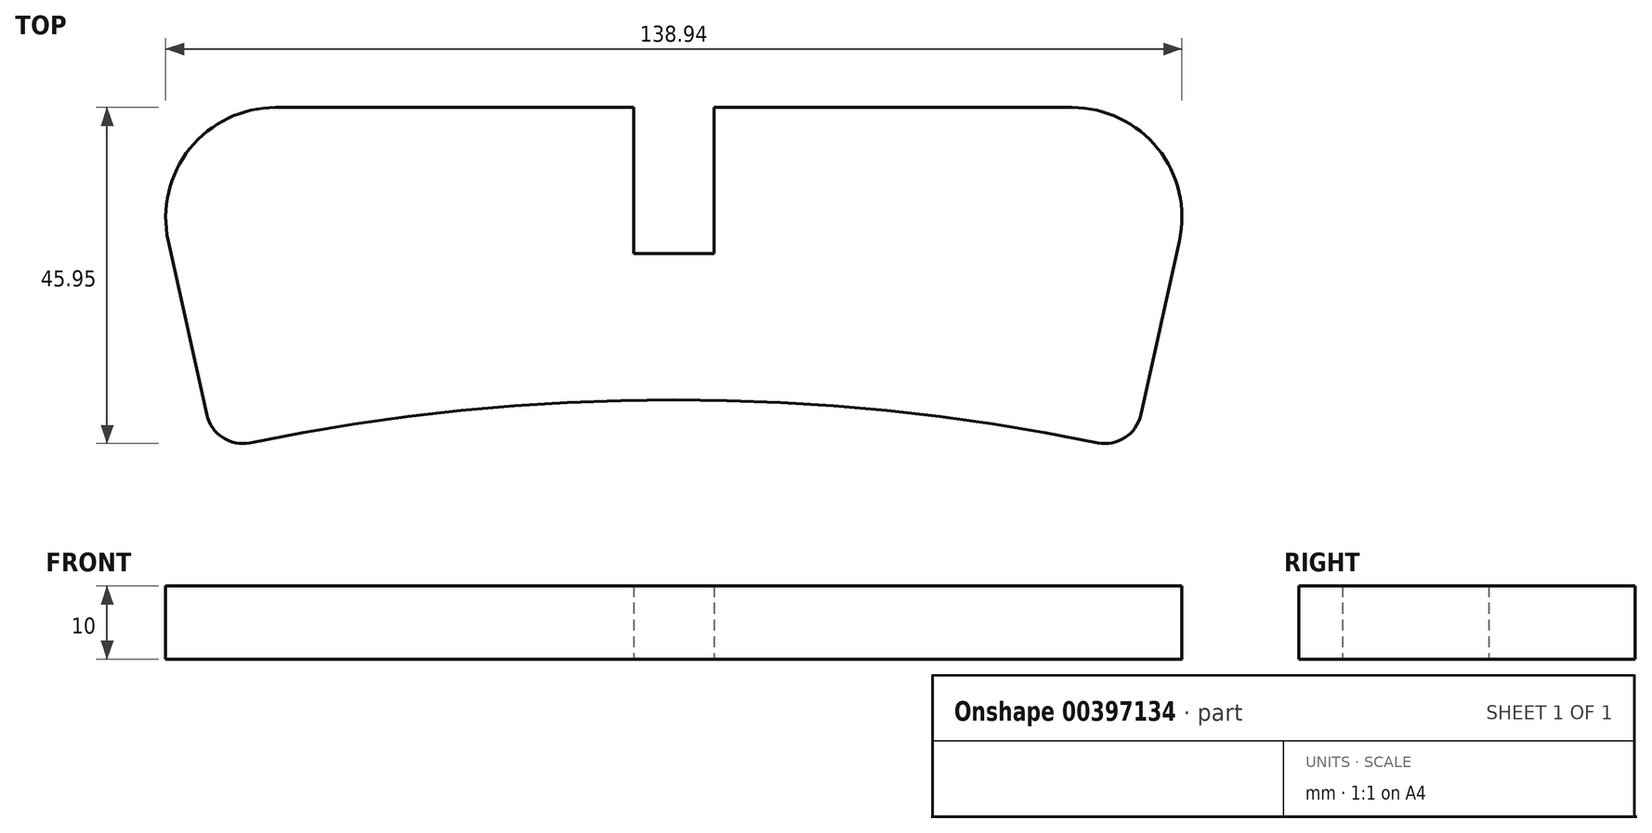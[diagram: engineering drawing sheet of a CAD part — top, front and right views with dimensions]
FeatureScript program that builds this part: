
annotation { "Feature Type Name" : "Feature", "Feature Type Description" : "" }
export const myFeature = defineFeature(function(context is Context, id is Id, definition is map)
    precondition{}
    {
        {
            var Q0;
            Q0=qCreatedBy(makeId("Top.planeOp"),FACE);
            var sketch = newSketch(context, id + "F0", { "sketchPlane" : qUnion([Q0])});
            skArc(sketch, "E0", {"start": v(57.96, 284.15) * mm, "mid": v(0, 290) * mm, "end": v(-57.96, 284.15) * mm});
            skLineSegment(sketch, "E1", {"start": v(0, 338.25) * mm, "end": v(0, 290) * mm, "construction": true});
            skLineSegment(sketch, "E2", {"start": v(-63.84, 287.97) * mm, "end": v(-69.11, 311.75) * mm});
            skLineSegment(sketch, "E3", {"start": v(63.84, 287.97) * mm, "end": v(69.11, 311.75) * mm});
            skLineSegment(sketch, "E4", {"start": v(-54.47, 330) * mm, "end": v(-5.5, 330) * mm});
            skLineSegment(sketch, "E5.top", {"start": v(5.5, 310) * mm, "end": v(-5.5, 310) * mm});
            skLineSegment(sketch, "E5.left", {"start": v(5.5, 330) * mm, "end": v(5.5, 310) * mm});
            skLineSegment(sketch, "E5.right", {"start": v(-5.5, 330) * mm, "end": v(-5.5, 310) * mm});
            skPoint(sketch, "E6.visualSharp", {"position": v(-73.16, 330) * mm});
            skArc(sketch, "E6.filletArc", {"start": v(-54.47, 330) * mm, "mid": v(-66.17, 324.39) * mm, "end": v(-69.11, 311.75) * mm});
            skPoint(sketch, "E7.visualSharp", {"position": v(73.16, 330) * mm});
            skArc(sketch, "E7.filletArc", {"start": v(69.11, 311.75) * mm, "mid": v(66.17, 324.39) * mm, "end": v(54.47, 330) * mm});
            skPoint(sketch, "E8.visualSharp", {"position": v(62.77, 283.13) * mm});
            skArc(sketch, "E8.filletArc", {"start": v(57.96, 284.15) * mm, "mid": v(61.68, 284.85) * mm, "end": v(63.84, 287.97) * mm});
            skPoint(sketch, "E9.visualSharp", {"position": v(-62.77, 283.13) * mm});
            skArc(sketch, "E9.filletArc", {"start": v(-63.84, 287.97) * mm, "mid": v(-61.68, 284.85) * mm, "end": v(-57.96, 284.15) * mm});
            skLineSegment(sketch, "E10.trimOffspring", {"start": v(5.5, 330) * mm, "end": v(54.47, 330) * mm});
            skSolve(sketch);
        }
        {
            var Q0;
            Q0 = qSketchRegion(id + "F0", true);
            extrude(context, id + "F1", {"entities" : qUnion([Q0]), "depth" : 10 * mm, "offsetDistance" : 25 * mm});
        }
    });
